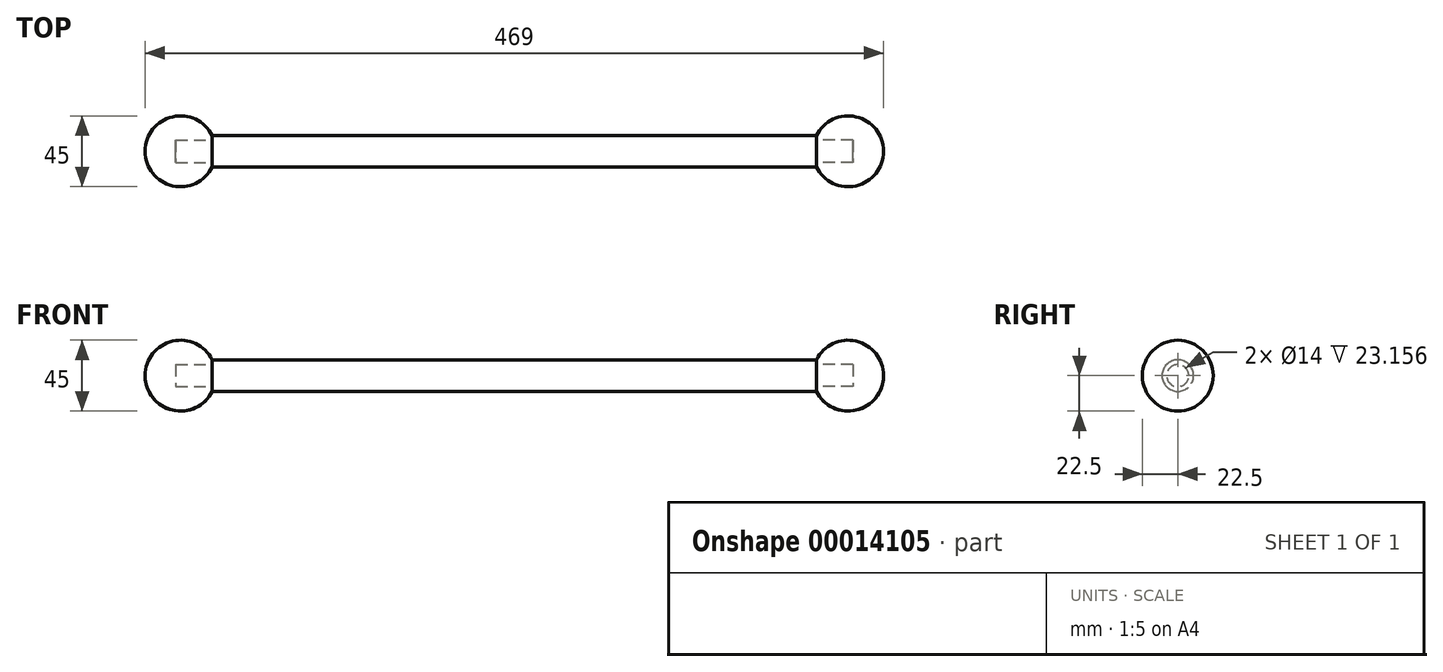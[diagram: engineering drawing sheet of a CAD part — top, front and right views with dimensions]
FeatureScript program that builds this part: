
annotation { "Feature Type Name" : "Feature", "Feature Type Description" : "" }
export const myFeature = defineFeature(function(context is Context, id is Id, definition is map)
    precondition{}
    {
        {
            var Q0;
            Q0=qCreatedBy(makeId("Front.planeOp"),FACE);
            var sketch = newSketch(context, id + "F0", { "sketchPlane" : qUnion([Q0])});
            skLineSegment(sketch, "E0", {"start": v(-215, 0) * mm, "end": v(215, 0) * mm});
            skLineSegment(sketch, "E1", {"start": v(215, 0) * mm, "end": v(215, 7) * mm});
            skLineSegment(sketch, "E2", {"start": v(215, 7) * mm, "end": v(191.84, 7) * mm});
            skLineSegment(sketch, "E3", {"start": v(191.84, 7) * mm, "end": v(191.84, 10) * mm});
            skLineSegment(sketch, "E4", {"start": v(191.84, 10) * mm, "end": v(-191.84, 10) * mm});
            skLineSegment(sketch, "E5", {"start": v(-191.84, 10) * mm, "end": v(-191.84, 7) * mm});
            skLineSegment(sketch, "E6", {"start": v(-191.84, 7) * mm, "end": v(-215, 7) * mm});
            skLineSegment(sketch, "E7", {"start": v(-215, 7) * mm, "end": v(-215, 0) * mm});
            skArc(sketch, "E8", {"start": v(234.5, 0) * mm, "mid": v(217.14, 21.9) * mm, "end": v(191.84, 10) * mm});
            skLineSegment(sketch, "E9", {"start": v(215, 0) * mm, "end": v(234.5, 0) * mm});
            skPoint(sketch, "E10.center.orphan", {"position": v(-212, 0) * mm});
            skSolve(sketch);
        }
        {
            var Q0;
            Q0=makeQuery(id+"F0.imprint","IMPRINT",FACE,{"disambiguationData":[TD([[makeQuery(id+"F0.imprint","IMPRINT",EDGE,{"derivedFrom":sQuery(id+"F0.wireOp",EDGE,"E0")}),1.0]])]});
            var Q1;
            Q1=sQuery(id+"F0.wireOp",EDGE,"E0");
            revolve(context, id + "F1", {"entities" : qUnion([Q0]), "axis" : qUnion([Q1]), "revolveType" : RevolveType.FULL});
        }
        {
            var Q0;
            Q0=makeQuery(id+"F0.imprint","IMPRINT",FACE,{"disambiguationData":[TD([[makeQuery(id+"F0.imprint","IMPRINT",EDGE,{"derivedFrom":sQuery(id+"F0.wireOp",EDGE,"E1")}),-1.0]])]});
            var Q1;
            Q1=sQuery(id+"F0.wireOp",EDGE,"E9");
            revolve(context, id + "F2", {"entities" : qUnion([Q0]), "axis" : qUnion([Q1]), "revolveType" : RevolveType.FULL});
        }
        {
            var Q0;
            Q0=makeQuery(id+"F2.opRevolve","SWEPT_BODY",BODY,{"disambiguationData":[OSD([sQuery(id+"F0.wireOp",EDGE,"E1"),sQuery(id+"F0.wireOp",EDGE,"E2"),sQuery(id+"F0.wireOp",EDGE,"E3"),sQuery(id+"F0.wireOp",EDGE,"E8"),sQuery(id+"F0.wireOp",EDGE,"E9")])]});
            var Q1;
            Q1=qCreatedBy(makeId("Right.planeOp"),FACE);
            mirror(context, id + "F3", {"entities" : qUnion([Q0]), "mirrorPlane" : qUnion([Q1])});
        }
    });
